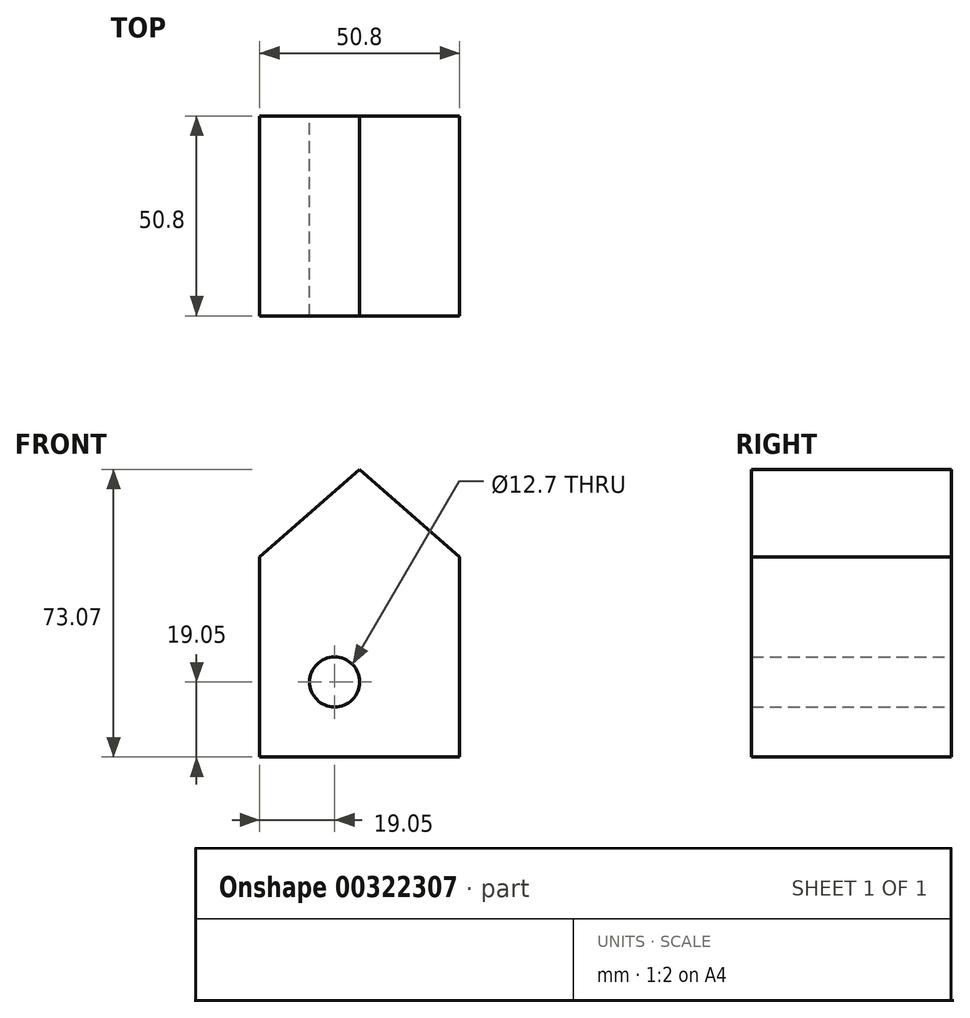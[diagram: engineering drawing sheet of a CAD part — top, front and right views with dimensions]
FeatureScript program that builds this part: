
annotation { "Feature Type Name" : "Feature", "Feature Type Description" : "" }
export const myFeature = defineFeature(function(context is Context, id is Id, definition is map)
    precondition{}
    {
        {
            var Q0;
            Q0=qCreatedBy(makeId("Front.planeOp"),FACE);
            var sketch = newSketch(context, id + "F0", { "sketchPlane" : qUnion([Q0])});
            skLineSegment(sketch, "E0.bottom", {"start": v(-25.4, -25.4) * mm, "end": v(25.4, -25.4) * mm});
            skLineSegment(sketch, "E0.top", {"start": v(-25.4, 25.4) * mm, "end": v(25.4, 25.4) * mm});
            skLineSegment(sketch, "E0.left", {"start": v(-25.4, -25.4) * mm, "end": v(-25.4, 25.4) * mm});
            skLineSegment(sketch, "E0.right", {"start": v(25.4, -25.4) * mm, "end": v(25.4, 25.4) * mm});
            skPoint(sketch, "E0.middle", {"position": v(0, 0) * mm});
            skLineSegment(sketch, "E1.bottom", {"start": v(-25.4, 25.4) * mm, "end": v(-25.4, 25.4) * mm});
            skLineSegment(sketch, "E1.top", {"start": v(-25.4, -25.4) * mm, "end": v(-25.4, -25.4) * mm});
            skLineSegment(sketch, "E1.left", {"start": v(-25.4, 25.4) * mm, "end": v(-25.4, -25.4) * mm});
            skLineSegment(sketch, "E1.right", {"start": v(-25.4, 25.4) * mm, "end": v(-25.4, -25.4) * mm});
            skLineSegment(sketch, "E2.left", {"start": v(-18.6, 25.4) * mm, "end": v(-18.6, 25.4) * mm});
            skPoint(sketch, "E2.middle", {"position": v(-25.4, 25.4) * mm});
            skLineSegment(sketch, "E3", {"start": v(-25.4, 25.4) * mm, "end": v(0, 47.67) * mm});
            skLineSegment(sketch, "E4", {"start": v(0, 47.67) * mm, "end": v(25.4, 25.4) * mm});
            skCircle(sketch, "E5", {"center": v(-6.35, -6.35) * mm, "radius": 6.35 * mm});
            skSolve(sketch);
        }
        {
            var Q0;
            Q0 = qSketchRegion(id + "F0", true);
            extrude(context, id + "F1", {"entities" : qUnion([Q0]), "depth" : 50.8 * mm});
        }
    });
